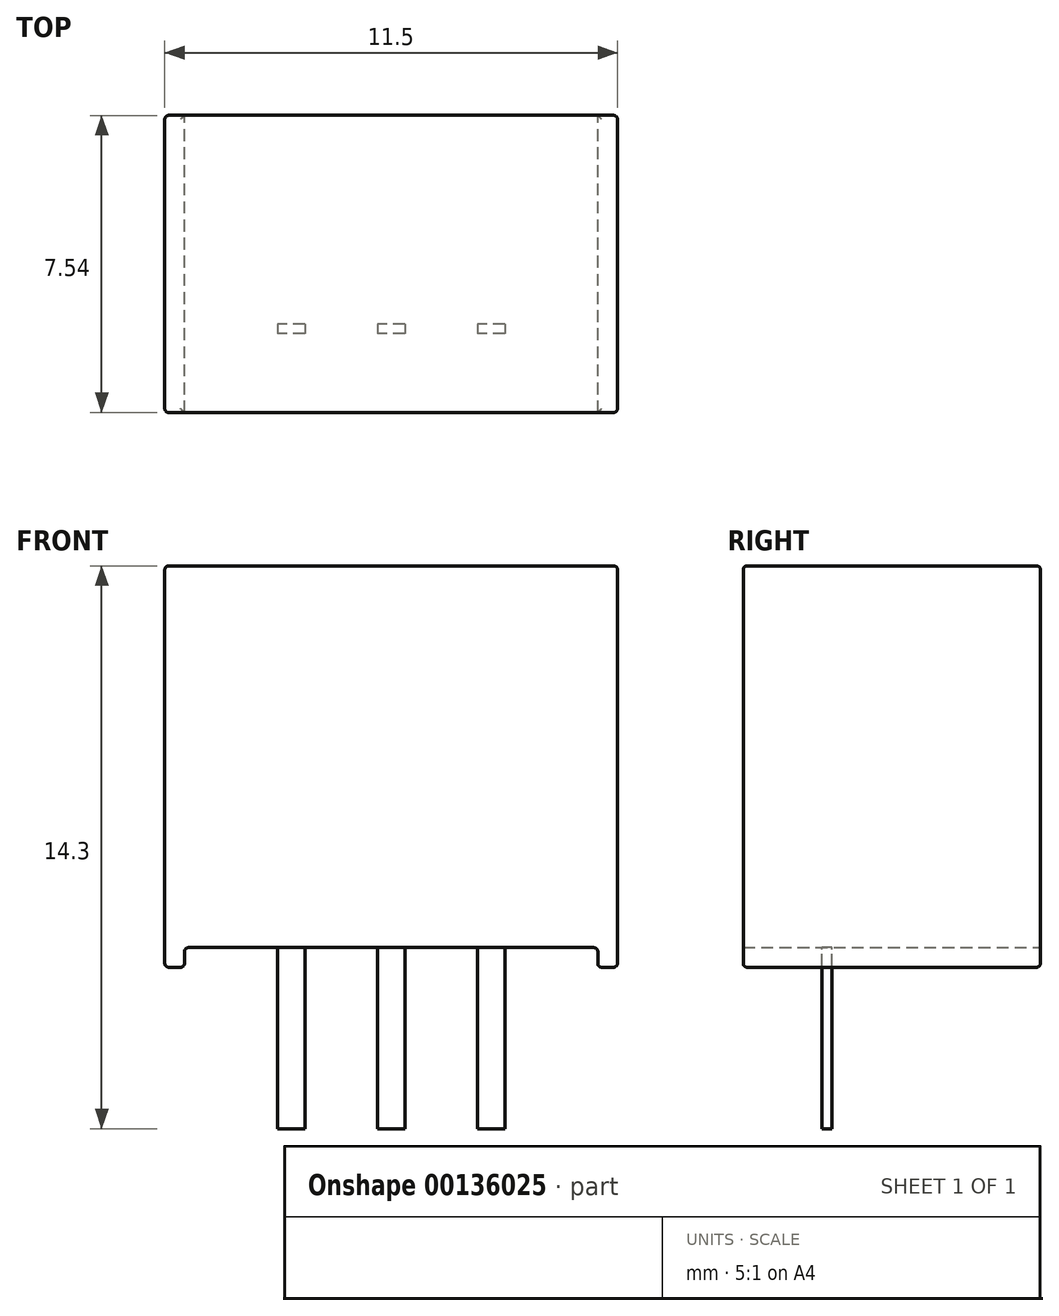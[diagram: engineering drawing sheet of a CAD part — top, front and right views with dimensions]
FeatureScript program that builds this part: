
annotation { "Feature Type Name" : "Feature", "Feature Type Description" : "" }
export const myFeature = defineFeature(function(context is Context, id is Id, definition is map)
    precondition{}
    {
        {
            var Q0;
            Q0=qCreatedBy(makeId("Top.planeOp"),FACE);
            var sketch = newSketch(context, id + "F0", { "sketchPlane" : qUnion([Q0])});
            skLineSegment(sketch, "E0.bottom", {"start": v(-5.75, 5.43) * mm, "end": v(5.75, 5.42) * mm});
            skLineSegment(sketch, "E0.top", {"start": v(-5.75, -2.12) * mm, "end": v(5.75, -2.12) * mm});
            skLineSegment(sketch, "E0.left", {"start": v(-5.75, 5.42) * mm, "end": v(-5.75, -2.12) * mm});
            skLineSegment(sketch, "E0.right", {"start": v(5.75, 5.42) * mm, "end": v(5.75, -2.12) * mm});
            skSolve(sketch);
        }
        {
            var Q0;
            Q0 = qSketchRegion(id + "F0", true);
            extrude(context, id + "F1", {"entities" : qUnion([Q0]), "depth" : 10.2 * mm});
        }
        {
            var Q0;
            Q0=makeQuery(id+"F1.opExtrude","CAP_FACE",FACE,{"disambiguationData":[OSD([sQuery(id+"F0.wireOp",EDGE,"E0.bottom"),sQuery(id+"F0.wireOp",EDGE,"E0.top"),sQuery(id+"F0.wireOp",EDGE,"E0.left"),sQuery(id+"F0.wireOp",EDGE,"E0.right")])],"isStart":true});
            var sketch = newSketch(context, id + "F2", { "sketchPlane" : qUnion([Q0])});
            skLineSegment(sketch, "E1", {"start": v(-5.75, 2.12) * mm, "end": v(-5.25, 2.12) * mm, "construction": true});
            skLineSegment(sketch, "E2", {"start": v(5.75, 2.12) * mm, "end": v(5.25, 2.12) * mm, "construction": true});
            skLineSegment(sketch, "E3.bottom", {"start": v(-5.25, 2.12) * mm, "end": v(5.25, 2.12) * mm});
            skLineSegment(sketch, "E3.top", {"start": v(-5.25, -5.43) * mm, "end": v(5.25, -5.43) * mm});
            skLineSegment(sketch, "E3.left", {"start": v(-5.25, 2.12) * mm, "end": v(-5.25, -5.43) * mm});
            skLineSegment(sketch, "E3.right", {"start": v(5.25, 2.12) * mm, "end": v(5.25, -5.42) * mm});
            skSolve(sketch);
        }
        {
            var Q0;
            Q0 = qSketchRegion(id + "F2", true);
            extrude(context, id + "F3", {"entities" : qUnion([Q0]), "operationType" : NewBodyOperationType.REMOVE, "oppositeDirection" : true, "depth" : .5 * mm});
        }
        {
            var Q0;
            Q0=makeQuery(id+"F1.opExtrude","CAP_EDGE",EDGE,{"disambiguationData":[OSD([sQuery(id+"F0.wireOp",EDGE,"E0.left")])],"isStart":true});
            var Q1;
            {var subQ0=sQuery(id+"F0.wireOp",EDGE,"E0.left");var subQ1=sQuery(id+"F0.wireOp",EDGE,"E0.top");Q1=makeQuery(id+"F3.boolean.opBoolean","SPLIT",EDGE,{"disambiguationData":[TD([makeQuery(id+"F1.opExtrude","SWEPT_FACE",FACE,{"disambiguationData":[OSD([subQ0])]})])],"derivedFrom":makeQuery(id+"F1.opExtrude","CAP_EDGE",EDGE,{"disambiguationData":[OSD([subQ1])],"isStart":true})});}
            var Q2;
            Q2=makeQuery(id+"F3.boolean.opBoolean","COPY",EDGE,{"derivedFrom":makeQuery(id+"F3.opExtrude","CAP_EDGE",EDGE,{"disambiguationData":[OSD([sQuery(id+"F2.wireOp",EDGE,"E3.left")])],"isStart":true})});
            var Q3;
            {var subQ0=sQuery(id+"F0.wireOp",EDGE,"E0.bottom");var subQ1=sQuery(id+"F0.wireOp",EDGE,"E0.left");Q3=makeQuery(id+"F3.boolean.opBoolean","SPLIT",EDGE,{"disambiguationData":[TD([makeQuery(id+"F1.opExtrude","SWEPT_FACE",FACE,{"disambiguationData":[OSD([subQ1])]})])],"derivedFrom":makeQuery(id+"F1.opExtrude","CAP_EDGE",EDGE,{"disambiguationData":[OSD([subQ0])],"isStart":true})});}
            var Q4;
            Q4=makeQuery(id+"F3.boolean.opBoolean","COPY",EDGE,{"derivedFrom":makeQuery(id+"F3.opExtrude","SWEPT_EDGE",EDGE,{"disambiguationData":[OSD([sQuery(id+"F0.wireOp",EDGE,"E0.bottom"),sQuery(id+"F2.wireOp",EDGE,"E3.top"),sQuery(id+"F2.wireOp",EDGE,"E3.left")])]})});
            var Q5;
            Q5=makeQuery(id+"F3.boolean.opBoolean","COPY",EDGE,{"derivedFrom":makeQuery(id+"F3.opExtrude","CAP_EDGE",EDGE,{"disambiguationData":[OSD([sQuery(id+"F2.wireOp",EDGE,"E3.left")])],"isStart":false})});
            var Q6;
            Q6=makeQuery(id+"F3.boolean.opBoolean","COPY",EDGE,{"derivedFrom":makeQuery(id+"F3.opExtrude","SWEPT_EDGE",EDGE,{"disambiguationData":[OSD([sQuery(id+"F0.wireOp",EDGE,"E0.top"),sQuery(id+"F2.wireOp",EDGE,"E3.bottom"),sQuery(id+"F2.wireOp",EDGE,"E3.left")])]})});
            var Q7;
            Q7=makeQuery(id+"F3.boolean.opBoolean","COPY",EDGE,{"derivedFrom":makeQuery(id+"F3.opExtrude","CAP_EDGE",EDGE,{"disambiguationData":[OSD([sQuery(id+"F2.wireOp",EDGE,"E3.bottom")])],"isStart":false})});
            var Q8;
            Q8=makeQuery(id+"F3.boolean.opBoolean","COPY",EDGE,{"derivedFrom":makeQuery(id+"F3.opExtrude","CAP_EDGE",EDGE,{"disambiguationData":[OSD([sQuery(id+"F2.wireOp",EDGE,"E3.top")])],"isStart":false})});
            var Q9;
            {var subQ0=sQuery(id+"F0.wireOp",EDGE,"E0.bottom");var subQ1=sQuery(id+"F0.wireOp",EDGE,"E0.top");var subQ2=sQuery(id+"F0.wireOp",EDGE,"E0.right");Q9=makeQuery(id+"F3.boolean.opBoolean","SPLIT",FACE,{"disambiguationData":[TD([makeQuery(id+"F1.opExtrude","SWEPT_FACE",FACE,{"disambiguationData":[OSD([subQ2])]})])],"derivedFrom":makeQuery(id+"F1.opExtrude","CAP_FACE",FACE,{"disambiguationData":[OSD([subQ0,subQ1,sQuery(id+"F0.wireOp",EDGE,"E0.left"),subQ2])],"isStart":true})});}
            var Q10;
            Q10=makeQuery(id+"F1.opExtrude","CAP_EDGE",EDGE,{"disambiguationData":[OSD([sQuery(id+"F0.wireOp",EDGE,"E0.right")])],"isStart":true});
            var Q11;
            {var subQ0=sQuery(id+"F0.wireOp",EDGE,"E0.bottom");var subQ1=sQuery(id+"F0.wireOp",EDGE,"E0.right");Q11=makeQuery(id+"F3.boolean.opBoolean","SPLIT",EDGE,{"disambiguationData":[TD([makeQuery(id+"F1.opExtrude","SWEPT_FACE",FACE,{"disambiguationData":[OSD([subQ1])]})])],"derivedFrom":makeQuery(id+"F1.opExtrude","CAP_EDGE",EDGE,{"disambiguationData":[OSD([subQ0])],"isStart":true})});}
            var Q12;
            {var subQ0=sQuery(id+"F0.wireOp",EDGE,"E0.right");var subQ1=sQuery(id+"F0.wireOp",EDGE,"E0.top");Q12=makeQuery(id+"F3.boolean.opBoolean","SPLIT",EDGE,{"disambiguationData":[TD([makeQuery(id+"F1.opExtrude","SWEPT_FACE",FACE,{"disambiguationData":[OSD([subQ0])]})])],"derivedFrom":makeQuery(id+"F1.opExtrude","CAP_EDGE",EDGE,{"disambiguationData":[OSD([subQ1])],"isStart":true})});}
            var Q13;
            Q13=makeQuery(id+"F1.opExtrude","SWEPT_EDGE",EDGE,{"disambiguationData":[OSD([sQuery(id+"F0.wireOp",EDGE,"E0.bottom"),sQuery(id+"F0.wireOp",EDGE,"E0.right")])]});
            var Q14;
            Q14=makeQuery(id+"F3.boolean.opBoolean","COPY",EDGE,{"derivedFrom":makeQuery(id+"F3.opExtrude","SWEPT_EDGE",EDGE,{"disambiguationData":[OSD([sQuery(id+"F0.wireOp",EDGE,"E0.bottom"),sQuery(id+"F2.wireOp",EDGE,"E3.top"),sQuery(id+"F2.wireOp",EDGE,"E3.right")])]})});
            var Q15;
            Q15=makeQuery(id+"F1.opExtrude","SWEPT_EDGE",EDGE,{"disambiguationData":[OSD([sQuery(id+"F0.wireOp",EDGE,"E0.top"),sQuery(id+"F0.wireOp",EDGE,"E0.right")])]});
            var Q16;
            Q16=makeQuery(id+"F3.boolean.opBoolean","COPY",EDGE,{"derivedFrom":makeQuery(id+"F3.opExtrude","SWEPT_EDGE",EDGE,{"disambiguationData":[OSD([sQuery(id+"F0.wireOp",EDGE,"E0.top"),sQuery(id+"F2.wireOp",EDGE,"E3.bottom"),sQuery(id+"F2.wireOp",EDGE,"E3.right")])]})});
            var Q17;
            Q17=makeQuery(id+"F3.boolean.opBoolean","COPY",EDGE,{"derivedFrom":makeQuery(id+"F3.opExtrude","CAP_EDGE",EDGE,{"disambiguationData":[OSD([sQuery(id+"F2.wireOp",EDGE,"E3.right")])],"isStart":false})});
            var Q18;
            Q18=makeQuery(id+"F1.opExtrude","SWEPT_EDGE",EDGE,{"disambiguationData":[OSD([sQuery(id+"F0.wireOp",EDGE,"E0.top"),sQuery(id+"F0.wireOp",EDGE,"E0.left")])]});
            var Q19;
            Q19=makeQuery(id+"F1.opExtrude","SWEPT_EDGE",EDGE,{"disambiguationData":[OSD([sQuery(id+"F0.wireOp",EDGE,"E0.bottom"),sQuery(id+"F0.wireOp",EDGE,"E0.left")])]});
            var Q20;
            Q20=makeQuery(id+"F1.opExtrude","CAP_EDGE",EDGE,{"disambiguationData":[OSD([sQuery(id+"F0.wireOp",EDGE,"E0.top")])],"isStart":false});
            var Q21;
            Q21=makeQuery(id+"F1.opExtrude","CAP_EDGE",EDGE,{"disambiguationData":[OSD([sQuery(id+"F0.wireOp",EDGE,"E0.right")])],"isStart":false});
            var Q22;
            Q22=makeQuery(id+"F1.opExtrude","CAP_EDGE",EDGE,{"disambiguationData":[OSD([sQuery(id+"F0.wireOp",EDGE,"E0.bottom")])],"isStart":false});
            var Q23;
            Q23=makeQuery(id+"F1.opExtrude","CAP_EDGE",EDGE,{"disambiguationData":[OSD([sQuery(id+"F0.wireOp",EDGE,"E0.left")])],"isStart":false});
            fillet(context, id + "F4", {"entities" : qUnion([Q0, Q1, Q2, Q3, Q4, Q5, Q6, Q7, Q8, Q9, Q10, Q11, Q12, Q13, Q14, Q15, Q16, Q17, Q18, Q19, Q20, Q21, Q22, Q23]), "radius" : 0.1 * mm, "tangentPropagation" : true, "allowEdgeOverflow" : false});
        }
        {
            var Q0;
            Q0=qCreatedBy(makeId("Top.planeOp"),FACE);
            var sketch = newSketch(context, id + "F5", { "sketchPlane" : qUnion([Q0])});
            skLineSegment(sketch, "E4.top", {"start": v(2.9, -0.13) * mm, "end": v(2.19, -0.13) * mm});
            skLineSegment(sketch, "E4.left", {"start": v(2.9, 0.12) * mm, "end": v(2.9, -0.13) * mm});
            skLineSegment(sketch, "E4.right", {"start": v(2.19, 0.12) * mm, "end": v(2.19, -0.13) * mm});
            skLineSegment(sketch, "E5.bottom", {"start": v(0.35, 0.12) * mm, "end": v(-0.35, 0.12) * mm});
            skLineSegment(sketch, "E5.top", {"start": v(0.35, -0.12) * mm, "end": v(-0.35, -0.12) * mm});
            skLineSegment(sketch, "E5.left", {"start": v(0.35, 0.12) * mm, "end": v(0.35, -0.12) * mm});
            skLineSegment(sketch, "E5.right", {"start": v(-0.35, 0.12) * mm, "end": v(-0.35, -0.12) * mm});
            skLineSegment(sketch, "E6.bottom", {"start": v(-2.19, 0.12) * mm, "end": v(-2.9, 0.13) * mm});
            skLineSegment(sketch, "E6.top", {"start": v(-2.19, -0.13) * mm, "end": v(-2.9, -0.12) * mm});
            skLineSegment(sketch, "E6.left", {"start": v(-2.19, 0.12) * mm, "end": v(-2.19, -0.13) * mm});
            skLineSegment(sketch, "E6.right", {"start": v(-2.9, 0.12) * mm, "end": v(-2.9, -0.13) * mm});
            skLineSegment(sketch, "E7", {"start": v(2.9, 0.13) * mm, "end": v(2.19, 0.13) * mm});
            skPoint(sketch, "E8", {"position": v(2.54, 0.13) * mm});
            skPoint(sketch, "E9", {"position": v(0, 0.12) * mm});
            skPoint(sketch, "E10", {"position": v(-2.54, 0.12) * mm});
            skLineSegment(sketch, "E11", {"start": v(2.54, 0.13) * mm, "end": v(0, 0.12) * mm, "construction": true});
            skLineSegment(sketch, "E12", {"start": v(0, 0.12) * mm, "end": v(-2.54, 0.12) * mm, "construction": true});
            skSolve(sketch);
        }
        {
            var Q0;
            Q0 = qSketchRegion(id + "F5", true);
            extrude(context, id + "F6", {"entities" : qUnion([Q0]), "oppositeDirection" : true, "depth" : 4.1 * mm, "hasSecondDirection" : true, "secondDirectionBound" : SecondDirectionBoundingType.UP_TO_NEXT, "secondDirectionOppositeDirection" : false, "secondDirectionDepth" : 25 * mm});
        }
    });
